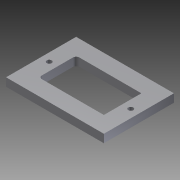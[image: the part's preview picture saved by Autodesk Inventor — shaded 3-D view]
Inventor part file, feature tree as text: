
AUTODESK INVENTOR PART (.ipt)
format: ipt  version: 2012 (Build 160160000, 160)  size: 87,552 bytes
history: native  units: mm
features: extrude x1, sketch x1
ambient origin geometry x8: Origin, YZ Plane, XZ Plane, XY Plane, X Axis, Y Axis, Z Axis, Center Point
bodies: Solid1 (feature_tree)
feature tree (2):
  extrude  "Extrusion1"  Depth=5.0mm TaperAngle=0.0deg
  sketch  "Sketch1"  dims[d0=2.0mm d1=43.0mm d2=3.0mm d3=5.0mm d4=21.5mm d5=3.0mm d6=5.0mm d7=21.5mm d8=5.0mm d9=0.0mm]
